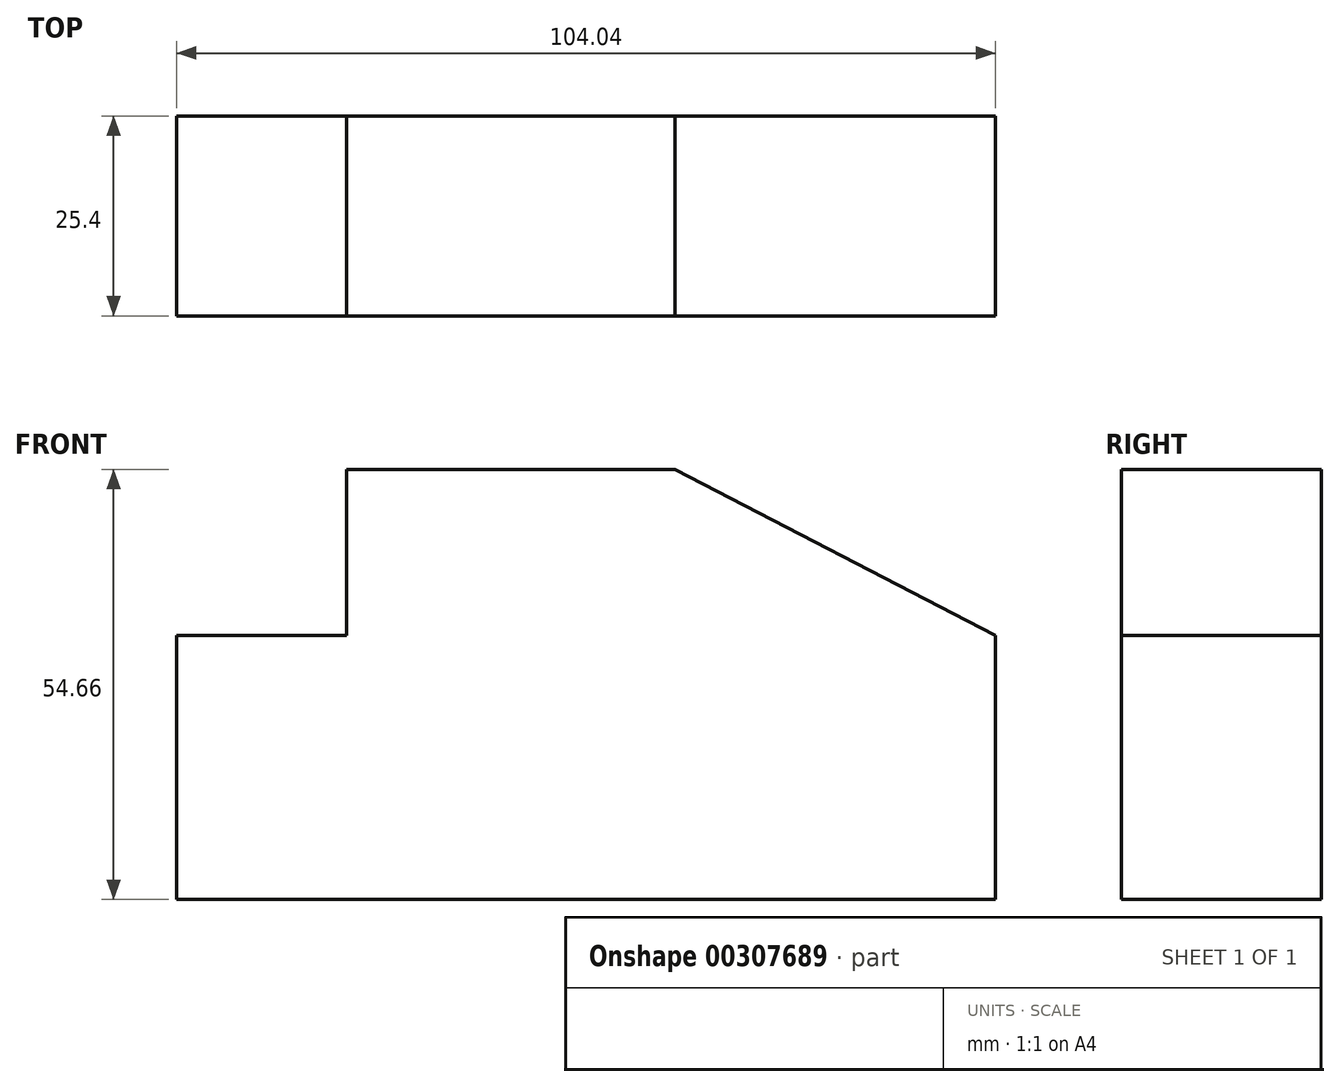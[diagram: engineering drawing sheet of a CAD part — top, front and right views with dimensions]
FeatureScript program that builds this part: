
annotation { "Feature Type Name" : "Feature", "Feature Type Description" : "" }
export const myFeature = defineFeature(function(context is Context, id is Id, definition is map)
    precondition{}
    {
        {
            var Q0;
            Q0=qCreatedBy(makeId("Front.planeOp"),FACE);
            var sketch = newSketch(context, id + "F0", { "sketchPlane" : qUnion([Q0])});
            skLineSegment(sketch, "E0", {"start": v(-55.62, -47.23) * mm, "end": v(48.42, -47.23) * mm});
            skLineSegment(sketch, "E1", {"start": v(48.42, -47.23) * mm, "end": v(48.42, -13.66) * mm});
            skLineSegment(sketch, "E2", {"start": v(48.42, -13.66) * mm, "end": v(7.67, 7.43) * mm});
            skLineSegment(sketch, "E3", {"start": v(7.67, 7.43) * mm, "end": v(-34.04, 7.43) * mm});
            skLineSegment(sketch, "E4", {"start": v(-34.04, 7.43) * mm, "end": v(-34.04, -13.66) * mm});
            skLineSegment(sketch, "E5", {"start": v(-34.04, -13.66) * mm, "end": v(-55.62, -13.66) * mm});
            skLineSegment(sketch, "E6", {"start": v(-55.62, -13.66) * mm, "end": v(-55.62, -47.23) * mm});
            skSolve(sketch);
        }
        {
            var Q0;
            Q0=makeQuery(id+"F0.imprint","IMPRINT",FACE,{"disambiguationData":[TD([[makeQuery(id+"F0.imprint","IMPRINT",EDGE,{"derivedFrom":sQuery(id+"F0.wireOp",EDGE,"E0")}),1.0]])]});
            extrude(context, id + "F1", {"entities" : qUnion([Q0]), "depth" : 25.4 * mm});
        }
    });
